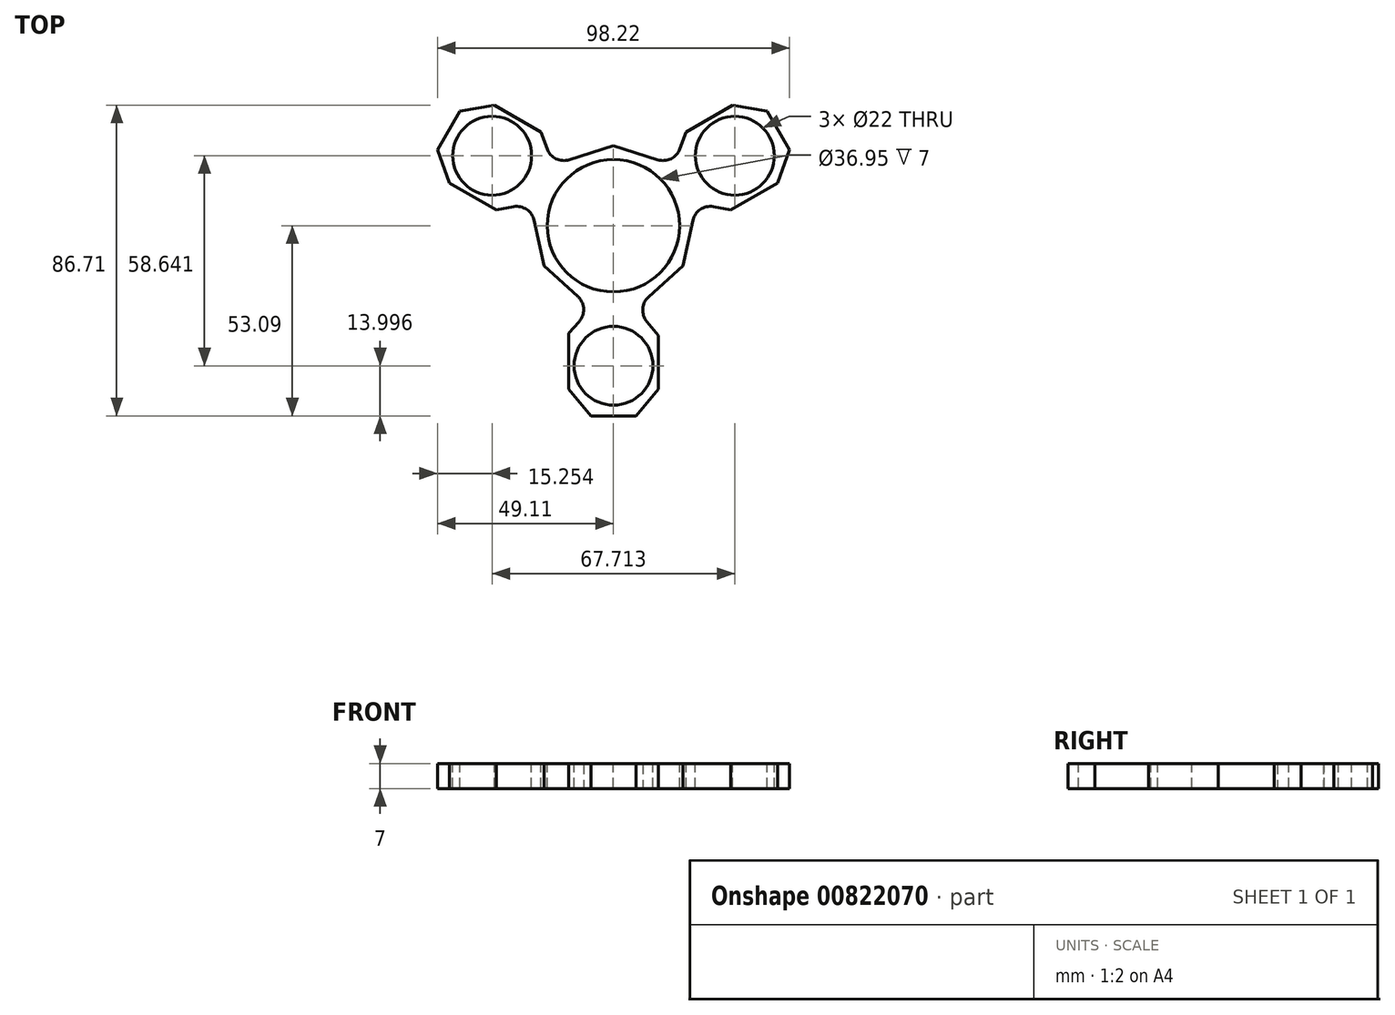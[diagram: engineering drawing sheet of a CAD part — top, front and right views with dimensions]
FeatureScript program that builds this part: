
annotation { "Feature Type Name" : "Feature", "Feature Type Description" : "" }
export const myFeature = defineFeature(function(context is Context, id is Id, definition is map)
    precondition{}
    {
        {
            var Q0;
            Q0=qCreatedBy(makeId("Top.planeOp"),FACE);
            var sketch = newSketch(context, id + "F0", { "sketchPlane" : qUnion([Q0])});
            skLineSegment(sketch, "E0", {"start": v(40, 0) * mm, "end": v(0, 69.28) * mm});
            skLineSegment(sketch, "E1", {"start": v(0, 69.28) * mm, "end": v(-40, 0) * mm});
            skLineSegment(sketch, "E2", {"start": v(40, 0) * mm, "end": v(-40, 0) * mm});
            skLineSegment(sketch, "E3", {"start": v(0, 69.28) * mm, "end": v(0, 0) * mm});
            skLineSegment(sketch, "E4", {"start": v(-40, 0) * mm, "end": v(20, 34.64) * mm});
            skLineSegment(sketch, "E5", {"start": v(40, 0) * mm, "end": v(-20, 34.64) * mm});
            skLineSegment(sketch, "E6", {"start": v(-20, 34.64) * mm, "end": v(0, 23.1) * mm});
            skSolve(sketch);
        }
        {
            var Q0;
            {var subQ3=sQuery(id+"F0.wireOp",EDGE,"E6");Q0=makeQuery(id+"F0.imprint","IMPRINT",FACE,{"disambiguationData":[TD([[makeQuery(id+"F0.imprint","IMPRINT",EDGE,{"derivedFrom":subQ3}),1.0]])]});}
            var Q1;
            {var subQ1=sQuery(id+"F0.wireOp",EDGE,"E0");var subQ3=sQuery(id+"F0.wireOp",EDGE,"E4");var subQ4=makeQuery(id+"F0.imprint","INTERSECT",VERTEX,{"derivedFrom":[subQ1,subQ3]});Q1=makeQuery(id+"F0.imprint","IMPRINT",FACE,{"disambiguationData":[TD([[makeQuery(id+"F0.imprint","IMPRINT",EDGE,{"disambiguationData":[TD([[subQ4,-1.0]])],"derivedFrom":subQ1}),1.0]])]});}
            var Q2;
            {var subQ0=sQuery(id+"F0.wireOp",EDGE,"E5");Q2=makeQuery(id+"F0.imprint","IMPRINT",FACE,{"disambiguationData":[TD([[makeQuery(id+"F0.imprint","IMPRINT",EDGE,{"derivedFrom":subQ0}),-1.0]])]});}
            var Q3;
            {var subQ0=sQuery(id+"F0.wireOp",EDGE,"E5");Q3=makeQuery(id+"F0.imprint","IMPRINT",FACE,{"disambiguationData":[TD([[makeQuery(id+"F0.imprint","IMPRINT",EDGE,{"derivedFrom":subQ0}),1.0]])]});}
            var Q4;
            {var subQ1=sQuery(id+"F0.wireOp",EDGE,"E2");var subQ3=sQuery(id+"F0.wireOp",EDGE,"E3");var subQ4=makeQuery(id+"F0.imprint","INTERSECT",VERTEX,{"derivedFrom":[subQ1,subQ3]});Q4=makeQuery(id+"F0.imprint","IMPRINT",FACE,{"disambiguationData":[TD([[makeQuery(id+"F0.imprint","IMPRINT",EDGE,{"disambiguationData":[TD([[subQ4,-1.0]])],"derivedFrom":subQ1}),-1.0]])]});}
            var Q5;
            {var subQ3=sQuery(id+"F0.wireOp",EDGE,"E6");Q5=makeQuery(id+"F0.imprint","IMPRINT",FACE,{"disambiguationData":[TD([[makeQuery(id+"F0.imprint","IMPRINT",EDGE,{"derivedFrom":subQ3}),-1.0]])]});}
            extrude(context, id + "F1", {"entities" : qUnion([Q0, Q1, Q2, Q3, Q4, Q5]), "depth" : 7 * mm, "offsetDistance" : 25 * mm});
        }
        {
            var Q0;
            Q0=makeQuery(id+"F1.opExtrude","SWEPT_BODY",BODY,{"disambiguationData":[OSD([sQuery(id+"F0.wireOp",EDGE,"E0"),sQuery(id+"F0.wireOp",EDGE,"E1"),sQuery(id+"F0.wireOp",EDGE,"E2")])]});
            var Q1;
            Q1=makeQuery(id+"F1.opExtrude","SWEPT_FACE",FACE,{"disambiguationData":[OSD([sQuery(id+"F0.wireOp",EDGE,"E2")])]});
            transform(context, id + "F2", {"entities" : qUnion([Q0]), "transformType" : TransformType.TRANSLATION_DISTANCE, "transformDirection" : qUnion([Q1]), "distance" : 23.1 * mm, "makeCopy" : false});
        }
        {
            var Q0;
            Q0=makeQuery(id+"F1.opExtrude","CAP_FACE",FACE,{"disambiguationData":[OSD([sQuery(id+"F0.wireOp",EDGE,"E0"),sQuery(id+"F0.wireOp",EDGE,"E1"),sQuery(id+"F0.wireOp",EDGE,"E2")])],"isStart":false});
            var sketch = newSketch(context, id + "F3", { "sketchPlane" : qUnion([Q0])});
            skCircle(sketch, "E7", {"center": v(0, 0) * mm, "radius": 18.48 * mm});
            skSolve(sketch);
        }
        {
            var Q0;
            Q0=makeQuery(id+"F3.imprint","IMPRINT",FACE,{"disambiguationData":[TD([[makeQuery(id+"F3.imprint","IMPRINT",EDGE,{"derivedFrom":sQuery(id+"F3.wireOp",EDGE,"E7")}),1.0]])]});
            extrude(context, id + "F4", {"entities" : qUnion([Q0]), "operationType" : NewBodyOperationType.REMOVE, "oppositeDirection" : true, "depth" : 25 * mm, "offsetDistance" : 25 * mm});
        }
        {
            var Q0;
            Q0=makeQuery(id+"F1.opExtrude","SWEPT_FACE",FACE,{"disambiguationData":[OSD([sQuery(id+"F0.wireOp",EDGE,"E2")])]});
            var sketch = newSketch(context, id + "F5", { "sketchPlane" : qUnion([Q0])});
            skPoint(sketch, "E8.middle", {"position": v(0, 0) * mm});
            skLineSegment(sketch, "E9", {"start": v(-12.5, 7) * mm, "end": v(12.5, 7) * mm});
            skPoint(sketch, "E9.endSnap0", {"position": v(12.5, 0) * mm});
            skLineSegment(sketch, "E10", {"start": v(12.5, 0) * mm, "end": v(-12.5, 0) * mm});
            skLineSegment(sketch, "E11", {"start": v(-12.5, 7) * mm, "end": v(-12.5, 0) * mm});
            skLineSegment(sketch, "E12", {"start": v(12.5, 0) * mm, "end": v(12.5, 7) * mm});
            skSolve(sketch);
        }
        {
            var Q0;
            Q0=makeQuery(id+"F5.imprint","IMPRINT",FACE,{"disambiguationData":[TD([[makeQuery(id+"F5.imprint","IMPRINT",EDGE,{"derivedFrom":sQuery(id+"F5.wireOp",EDGE,"E9")}),1.0]])]});
            extrude(context, id + "F6", {"entities" : qUnion([Q0]), "operationType" : NewBodyOperationType.ADD, "depth" : 30 * mm, "offsetDistance" : 25 * mm});
        }
        {
            var Q0;
            Q0=makeQuery(id+"F1.opExtrude","SWEPT_FACE",FACE,{"disambiguationData":[OSD([sQuery(id+"F0.wireOp",EDGE,"E0")])]});
            var sketch = newSketch(context, id + "F7", { "sketchPlane" : qUnion([Q0])});
            skLineSegment(sketch, "E13.bottom", {"start": v(12.5, 7) * mm, "end": v(-12.5, 7) * mm});
            skPoint(sketch, "E13.middle", {"position": v(0, 0) * mm});
            skLineSegment(sketch, "E14", {"start": v(-12.5, 0) * mm, "end": v(12.5, 0) * mm});
            skLineSegment(sketch, "E15", {"start": v(-12.5, 7) * mm, "end": v(-12.5, 0) * mm});
            skLineSegment(sketch, "E16", {"start": v(12.5, 7) * mm, "end": v(12.5, 0) * mm});
            skSolve(sketch);
        }
        {
            var Q0;
            Q0 = qSketchRegion(id + "F7", true);
            extrude(context, id + "F8", {"entities" : qUnion([Q0]), "operationType" : NewBodyOperationType.ADD, "depth" : 30 * mm, "offsetDistance" : 25 * mm});
        }
        {
            var Q0;
            Q0=makeQuery(id+"F1.opExtrude","SWEPT_FACE",FACE,{"disambiguationData":[OSD([sQuery(id+"F0.wireOp",EDGE,"E1")])]});
            var sketch = newSketch(context, id + "F9", { "sketchPlane" : qUnion([Q0])});
            skLineSegment(sketch, "E17.bottom", {"start": v(12.5, 0) * mm, "end": v(-12.5, 0) * mm});
            skPoint(sketch, "E17.middle", {"position": v(0, 1.96) * mm});
            skLineSegment(sketch, "E18", {"start": v(-12.5, 0) * mm, "end": v(-12.5, 7) * mm});
            skLineSegment(sketch, "E19", {"start": v(12.5, 0) * mm, "end": v(12.5, 7) * mm});
            skLineSegment(sketch, "E20", {"start": v(12.5, 7) * mm, "end": v(-12.5, 7) * mm});
            skLineSegment(sketch, "E21", {"start": v(-12.5, 7) * mm, "end": v(12.5, 7) * mm});
            skSolve(sketch);
        }
        {
            var Q0;
            Q0=makeQuery(id+"F9.imprint","IMPRINT",FACE,{"disambiguationData":[TD([[makeQuery(id+"F9.imprint","IMPRINT",EDGE,{"derivedFrom":sQuery(id+"F9.wireOp",EDGE,"E17.bottom")}),1.0]])]});
            extrude(context, id + "F10", {"entities" : qUnion([Q0]), "operationType" : NewBodyOperationType.ADD, "depth" : 30 * mm, "offsetDistance" : 25 * mm});
        }
        {
            var Q0;
            Q0=makeQuery(id+"F10.boolean.opBoolean","MERGE",FACE,{"derivedFrom":[makeQuery(id+"F8.boolean.opBoolean","MERGE",FACE,{"derivedFrom":[makeQuery(id+"F6.boolean.opBoolean","MERGE",FACE,{"derivedFrom":[makeQuery(id+"F1.opExtrude","CAP_FACE",FACE,{"disambiguationData":[OSD([sQuery(id+"F0.wireOp",EDGE,"E0"),sQuery(id+"F0.wireOp",EDGE,"E1"),sQuery(id+"F0.wireOp",EDGE,"E2")])],"isStart":false}),makeQuery(id+"F6.opExtrude","SWEPT_FACE",FACE,{"disambiguationData":[OSD([sQuery(id+"F5.wireOp",EDGE,"E9")])]})]}),makeQuery(id+"F8.opExtrude","SWEPT_FACE",FACE,{"disambiguationData":[OSD([sQuery(id+"F7.wireOp",EDGE,"E13.bottom")])]})]}),makeQuery(id+"F10.opExtrude","SWEPT_FACE",FACE,{"disambiguationData":[OSD([sQuery(id+"F9.wireOp",EDGE,"E21")])]})]});
            var sketch = newSketch(context, id + "F11", { "sketchPlane" : qUnion([Q0])});
            skLineSegment(sketch, "E22", {"start": v(-26.25, 0.72) * mm, "end": v(-12.5, -23.1) * mm});
            skLineSegment(sketch, "E23", {"start": v(-13.75, 22.37) * mm, "end": v(13.75, 22.37) * mm});
            skLineSegment(sketch, "E24", {"start": v(26.25, 0.72) * mm, "end": v(12.5, -23.1) * mm});
            skSolve(sketch);
        }
        {
            var Q0;
            Q0 = qSketchRegion(id + "F11", true);
            var Q1;
            Q1=makeQuery(id+"F11.imprint","IMPRINT",FACE,{"disambiguationData":[TD([[makeQuery(id+"F11.imprint","IMPRINT",EDGE,{"derivedFrom":sQuery(id+"F11.wireOp",EDGE,"E23")}),1.0]])]});
            var Q2;
            Q2=makeQuery(id+"F11.imprint","IMPRINT",FACE,{"disambiguationData":[TD([[makeQuery(id+"F11.imprint","IMPRINT",EDGE,{"derivedFrom":sQuery(id+"F11.wireOp",EDGE,"E24")}),1.0]])]});
            var Q3;
            Q3=makeQuery(id+"F11.imprint","IMPRINT",FACE,{"disambiguationData":[TD([[makeQuery(id+"F11.imprint","IMPRINT",EDGE,{"derivedFrom":sQuery(id+"F11.wireOp",EDGE,"E22")}),-1.0]])]});
            extrude(context, id + "F12", {"entities" : qUnion([Q0, Q1, Q2, Q3]), "operationType" : NewBodyOperationType.REMOVE, "oppositeDirection" : true, "depth" : 25 * mm, "offsetDistance" : 25 * mm});
        }
        {
            var Q0;
            Q0=makeQuery(id+"F10.boolean.opBoolean","MERGE",FACE,{"derivedFrom":[makeQuery(id+"F8.boolean.opBoolean","MERGE",FACE,{"derivedFrom":[makeQuery(id+"F6.boolean.opBoolean","MERGE",FACE,{"derivedFrom":[makeQuery(id+"F1.opExtrude","CAP_FACE",FACE,{"disambiguationData":[OSD([sQuery(id+"F0.wireOp",EDGE,"E0"),sQuery(id+"F0.wireOp",EDGE,"E1"),sQuery(id+"F0.wireOp",EDGE,"E2")])],"isStart":false}),makeQuery(id+"F6.opExtrude","SWEPT_FACE",FACE,{"disambiguationData":[OSD([sQuery(id+"F5.wireOp",EDGE,"E9")])]})]}),makeQuery(id+"F8.opExtrude","SWEPT_FACE",FACE,{"disambiguationData":[OSD([sQuery(id+"F7.wireOp",EDGE,"E13.bottom")])]})]}),makeQuery(id+"F10.opExtrude","SWEPT_FACE",FACE,{"disambiguationData":[OSD([sQuery(id+"F9.wireOp",EDGE,"E21")])]})]});
            var sketch = newSketch(context, id + "F13", { "sketchPlane" : qUnion([Q0])});
            skLineSegment(sketch, "E25", {"start": v(0, -53.1) * mm, "end": v(0, -50.1) * mm});
            skLineSegment(sketch, "E26", {"start": v(0, -53.1) * mm, "end": v(0, -39.1) * mm});
            skCircle(sketch, "E27", {"center": v(0, -39.1) * mm, "radius": 11 * mm});
            skLineSegment(sketch, "E28", {"start": v(-45.98, 26.55) * mm, "end": v(-33.86, 19.55) * mm});
            skLineSegment(sketch, "E29", {"start": v(45.98, 26.55) * mm, "end": v(33.86, 19.55) * mm});
            skCircle(sketch, "E30", {"center": v(-33.86, 19.55) * mm, "radius": 11 * mm});
            skCircle(sketch, "E31", {"center": v(33.86, 19.55) * mm, "radius": 11 * mm});
            skSolve(sketch);
        }
        {
            var Q0;
            Q0=makeQuery(id+"F13.imprint","IMPRINT",FACE,{"disambiguationData":[TD([[makeQuery(id+"F13.imprint","IMPRINT",EDGE,{"derivedFrom":sQuery(id+"F13.wireOp",EDGE,"E30")}),1.0]])]});
            var Q1;
            Q1=makeQuery(id+"F13.imprint","IMPRINT",FACE,{"disambiguationData":[TD([[makeQuery(id+"F13.imprint","IMPRINT",EDGE,{"derivedFrom":sQuery(id+"F13.wireOp",EDGE,"E31")}),1.0]])]});
            var Q2;
            Q2=makeQuery(id+"F13.imprint","IMPRINT",FACE,{"disambiguationData":[TD([[makeQuery(id+"F13.imprint","IMPRINT",EDGE,{"derivedFrom":sQuery(id+"F13.wireOp",EDGE,"E27")}),1.0]])]});
            extrude(context, id + "F14", {"entities" : qUnion([Q0, Q1, Q2]), "operationType" : NewBodyOperationType.REMOVE, "oppositeDirection" : true, "depth" : 25 * mm, "offsetDistance" : 25 * mm});
        }
        {
            var Q0;
            Q0=makeQuery(id+"F10.boolean.opBoolean","MERGE",FACE,{"derivedFrom":[makeQuery(id+"F8.boolean.opBoolean","MERGE",FACE,{"derivedFrom":[makeQuery(id+"F6.boolean.opBoolean","MERGE",FACE,{"derivedFrom":[makeQuery(id+"F1.opExtrude","CAP_FACE",FACE,{"disambiguationData":[OSD([sQuery(id+"F0.wireOp",EDGE,"E0"),sQuery(id+"F0.wireOp",EDGE,"E1"),sQuery(id+"F0.wireOp",EDGE,"E2")])],"isStart":false}),makeQuery(id+"F6.opExtrude","SWEPT_FACE",FACE,{"disambiguationData":[OSD([sQuery(id+"F5.wireOp",EDGE,"E9")])]})]}),makeQuery(id+"F8.opExtrude","SWEPT_FACE",FACE,{"disambiguationData":[OSD([sQuery(id+"F7.wireOp",EDGE,"E13.bottom")])]})]}),makeQuery(id+"F10.opExtrude","SWEPT_FACE",FACE,{"disambiguationData":[OSD([sQuery(id+"F9.wireOp",EDGE,"E21")])]})]});
            var sketch = newSketch(context, id + "F15", { "sketchPlane" : qUnion([Q0])});
            skLineSegment(sketch, "E32", {"start": v(-26.25, 0.72) * mm, "end": v(-13.75, 22.37) * mm});
            skLineSegment(sketch, "E33", {"start": v(13.75, 22.37) * mm, "end": v(26.25, 0.72) * mm});
            skLineSegment(sketch, "E34", {"start": v(12.5, -23.1) * mm, "end": v(-12.5, -23.1) * mm});
            skLineSegment(sketch, "E35", {"start": v(-26.25, 0.72) * mm, "end": v(-20, 11.55) * mm});
            skLineSegment(sketch, "E36", {"start": v(-20, 11.55) * mm, "end": v(-13.75, 22.37) * mm});
            skLineSegment(sketch, "E37", {"start": v(13.75, 22.37) * mm, "end": v(20, 11.55) * mm});
            skLineSegment(sketch, "E38", {"start": v(20, 11.55) * mm, "end": v(26.25, 0.72) * mm});
            skLineSegment(sketch, "E39", {"start": v(12.5, -23.1) * mm, "end": v(0, -23.1) * mm});
            skLineSegment(sketch, "E40", {"start": v(0, -23.1) * mm, "end": v(-12.5, -23.1) * mm});
            skLineSegment(sketch, "E41", {"start": v(-26.74, 29.87) * mm, "end": v(-13.75, 22.37) * mm});
            skLineSegment(sketch, "E42", {"start": v(-39.24, 8.22) * mm, "end": v(-26.25, 0.72) * mm});
            skLineSegment(sketch, "E43", {"start": v(-12.5, -38.1) * mm, "end": v(-12.5, -23.1) * mm});
            skLineSegment(sketch, "E44", {"start": v(12.5, -38.1) * mm, "end": v(12.5, -23.1) * mm});
            skLineSegment(sketch, "E45", {"start": v(39.24, 8.22) * mm, "end": v(26.25, 0.72) * mm});
            skLineSegment(sketch, "E46", {"start": v(13.75, 22.37) * mm, "end": v(26.74, 29.87) * mm});
            skLineSegment(sketch, "E47", {"start": v(-20.25, 26.12) * mm, "end": v(-16.88, 16.96) * mm});
            skLineSegment(sketch, "E48", {"start": v(-16.88, 16.96) * mm, "end": v(0, 22.37) * mm});
            skLineSegment(sketch, "E49", {"start": v(0, 22.37) * mm, "end": v(16.87, 16.96) * mm});
            skLineSegment(sketch, "E50", {"start": v(16.87, 16.96) * mm, "end": v(20.25, 26.12) * mm});
            skLineSegment(sketch, "E51", {"start": v(-32.75, 4.47) * mm, "end": v(-23.13, 6.13) * mm});
            skLineSegment(sketch, "E52", {"start": v(-23.13, 6.13) * mm, "end": v(-19.38, -11.19) * mm});
            skLineSegment(sketch, "E53", {"start": v(-19.38, -11.19) * mm, "end": v(-6.25, -23.1) * mm});
            skLineSegment(sketch, "E54", {"start": v(-6.25, -23.1) * mm, "end": v(-12.5, -29.98) * mm});
            skLineSegment(sketch, "E55", {"start": v(12.5, -30.6) * mm, "end": v(6.25, -23.1) * mm});
            skLineSegment(sketch, "E56", {"start": v(6.25, -23.1) * mm, "end": v(19.38, -11.19) * mm});
            skLineSegment(sketch, "E57", {"start": v(19.38, -11.19) * mm, "end": v(23.12, 6.13) * mm});
            skLineSegment(sketch, "E58", {"start": v(23.12, 6.13) * mm, "end": v(32.75, 4.47) * mm});
            skLineSegment(sketch, "E59", {"start": v(-52.23, 15.72) * mm, "end": v(-39.24, 8.22) * mm});
            skLineSegment(sketch, "E60", {"start": v(-39.73, 37.37) * mm, "end": v(-26.74, 29.87) * mm});
            skLineSegment(sketch, "E61", {"start": v(39.73, 37.37) * mm, "end": v(26.74, 29.87) * mm});
            skLineSegment(sketch, "E62", {"start": v(52.23, 15.72) * mm, "end": v(39.24, 8.22) * mm});
            skLineSegment(sketch, "E63", {"start": v(12.5, -53.1) * mm, "end": v(12.5, -38.1) * mm});
            skLineSegment(sketch, "E64", {"start": v(-12.5, -53.1) * mm, "end": v(-12.5, -38.1) * mm});
            skLineSegment(sketch, "E65", {"start": v(-12.5, -53.1) * mm, "end": v(0, -53.1) * mm});
            skLineSegment(sketch, "E66", {"start": v(0, -53.1) * mm, "end": v(12.5, -53.1) * mm});
            skLineSegment(sketch, "E67", {"start": v(-39.73, 37.37) * mm, "end": v(-45.98, 26.55) * mm});
            skLineSegment(sketch, "E68", {"start": v(-45.98, 26.55) * mm, "end": v(-52.23, 15.72) * mm});
            skLineSegment(sketch, "E69", {"start": v(39.73, 37.37) * mm, "end": v(45.98, 26.55) * mm});
            skLineSegment(sketch, "E70", {"start": v(45.98, 26.55) * mm, "end": v(52.23, 15.72) * mm});
            skLineSegment(sketch, "E71", {"start": v(33.24, 33.62) * mm, "end": v(42.86, 31.96) * mm});
            skLineSegment(sketch, "E72", {"start": v(42.86, 31.96) * mm, "end": v(49.1, 21.13) * mm});
            skLineSegment(sketch, "E73", {"start": v(49.1, 21.13) * mm, "end": v(45.74, 11.97) * mm});
            skLineSegment(sketch, "E74", {"start": v(-42.86, 31.96) * mm, "end": v(-33.24, 33.62) * mm});
            skLineSegment(sketch, "E75", {"start": v(-49.1, 21.13) * mm, "end": v(-45.74, 11.97) * mm});
            skLineSegment(sketch, "E76", {"start": v(-12.5, -45.6) * mm, "end": v(-6.25, -53.1) * mm});
            skLineSegment(sketch, "E77", {"start": v(-6.25, -53.1) * mm, "end": v(6.25, -53.1) * mm});
            skLineSegment(sketch, "E78", {"start": v(6.25, -53.1) * mm, "end": v(12.5, -45.6) * mm});
            skSolve(sketch);
        }
        {
            var Q0;
            {var subQ3=sQuery(id+"F15.wireOp",EDGE,"E47");Q0=makeQuery(id+"F15.imprint","IMPRINT",FACE,{"disambiguationData":[TD([[makeQuery(id+"F15.imprint","IMPRINT",EDGE,{"derivedFrom":subQ3}),1.0]])]});}
            var Q1;
            {var subQ3=sQuery(id+"F15.wireOp",EDGE,"E48");Q1=makeQuery(id+"F15.imprint","IMPRINT",FACE,{"disambiguationData":[TD([[makeQuery(id+"F15.imprint","IMPRINT",EDGE,{"derivedFrom":subQ3}),1.0]])]});}
            var Q2;
            {var subQ3=sQuery(id+"F15.wireOp",EDGE,"E49");Q2=makeQuery(id+"F15.imprint","IMPRINT",FACE,{"disambiguationData":[TD([[makeQuery(id+"F15.imprint","IMPRINT",EDGE,{"derivedFrom":subQ3}),1.0]])]});}
            var Q3;
            {var subQ3=sQuery(id+"F15.wireOp",EDGE,"E50");Q3=makeQuery(id+"F15.imprint","IMPRINT",FACE,{"disambiguationData":[TD([[makeQuery(id+"F15.imprint","IMPRINT",EDGE,{"derivedFrom":subQ3}),1.0]])]});}
            var Q4;
            {var subQ3=sQuery(id+"F15.wireOp",EDGE,"E58");Q4=makeQuery(id+"F15.imprint","IMPRINT",FACE,{"disambiguationData":[TD([[makeQuery(id+"F15.imprint","IMPRINT",EDGE,{"derivedFrom":subQ3}),-1.0]])]});}
            var Q5;
            {var subQ3=sQuery(id+"F15.wireOp",EDGE,"E57");Q5=makeQuery(id+"F15.imprint","IMPRINT",FACE,{"disambiguationData":[TD([[makeQuery(id+"F15.imprint","IMPRINT",EDGE,{"derivedFrom":subQ3}),-1.0]])]});}
            var Q6;
            {var subQ3=sQuery(id+"F15.wireOp",EDGE,"E56");Q6=makeQuery(id+"F15.imprint","IMPRINT",FACE,{"disambiguationData":[TD([[makeQuery(id+"F15.imprint","IMPRINT",EDGE,{"derivedFrom":subQ3}),-1.0]])]});}
            var Q7;
            {var subQ3=sQuery(id+"F15.wireOp",EDGE,"E55");Q7=makeQuery(id+"F15.imprint","IMPRINT",FACE,{"disambiguationData":[TD([[makeQuery(id+"F15.imprint","IMPRINT",EDGE,{"derivedFrom":subQ3}),-1.0]])]});}
            var Q8;
            {var subQ3=sQuery(id+"F15.wireOp",EDGE,"E54");Q8=makeQuery(id+"F15.imprint","IMPRINT",FACE,{"disambiguationData":[TD([[makeQuery(id+"F15.imprint","IMPRINT",EDGE,{"derivedFrom":subQ3}),-1.0]])]});}
            var Q9;
            {var subQ3=sQuery(id+"F15.wireOp",EDGE,"E53");Q9=makeQuery(id+"F15.imprint","IMPRINT",FACE,{"disambiguationData":[TD([[makeQuery(id+"F15.imprint","IMPRINT",EDGE,{"derivedFrom":subQ3}),-1.0]])]});}
            var Q10;
            {var subQ3=sQuery(id+"F15.wireOp",EDGE,"E52");Q10=makeQuery(id+"F15.imprint","IMPRINT",FACE,{"disambiguationData":[TD([[makeQuery(id+"F15.imprint","IMPRINT",EDGE,{"derivedFrom":subQ3}),-1.0]])]});}
            var Q11;
            {var subQ3=sQuery(id+"F15.wireOp",EDGE,"E51");Q11=makeQuery(id+"F15.imprint","IMPRINT",FACE,{"disambiguationData":[TD([[makeQuery(id+"F15.imprint","IMPRINT",EDGE,{"derivedFrom":subQ3}),-1.0]])]});}
            var Q12;
            {var subQ3=sQuery(id+"F15.wireOp",EDGE,"E75");Q12=makeQuery(id+"F15.imprint","IMPRINT",FACE,{"disambiguationData":[TD([[makeQuery(id+"F15.imprint","IMPRINT",EDGE,{"derivedFrom":subQ3}),-1.0]])]});}
            var Q13;
            {var subQ3=sQuery(id+"F15.wireOp",EDGE,"E74");Q13=makeQuery(id+"F15.imprint","IMPRINT",FACE,{"disambiguationData":[TD([[makeQuery(id+"F15.imprint","IMPRINT",EDGE,{"derivedFrom":subQ3}),1.0]])]});}
            var Q14;
            {var subQ0=sQuery(id+"F15.wireOp",EDGE,"E69");Q14=makeQuery(id+"F15.imprint","IMPRINT",FACE,{"disambiguationData":[TD([[makeQuery(id+"F15.imprint","IMPRINT",EDGE,{"derivedFrom":subQ0}),1.0]])]});}
            var Q15;
            {var subQ0=sQuery(id+"F15.wireOp",EDGE,"E70");Q15=makeQuery(id+"F15.imprint","IMPRINT",FACE,{"disambiguationData":[TD([[makeQuery(id+"F15.imprint","IMPRINT",EDGE,{"derivedFrom":subQ0}),1.0]])]});}
            var Q16;
            {var subQ0=sQuery(id+"F15.wireOp",EDGE,"E66");Q16=makeQuery(id+"F15.imprint","IMPRINT",FACE,{"disambiguationData":[TD([[makeQuery(id+"F15.imprint","IMPRINT",EDGE,{"derivedFrom":subQ0}),-1.0]])]});}
            var Q17;
            {var subQ0=sQuery(id+"F15.wireOp",EDGE,"E65");Q17=makeQuery(id+"F15.imprint","IMPRINT",FACE,{"disambiguationData":[TD([[makeQuery(id+"F15.imprint","IMPRINT",EDGE,{"derivedFrom":subQ0}),-1.0]])]});}
            extrude(context, id + "F16", {"entities" : qUnion([Q0, Q1, Q2, Q3, Q4, Q5, Q6, Q7, Q8, Q9, Q10, Q11, Q12, Q13, Q14, Q15, Q16, Q17]), "operationType" : NewBodyOperationType.REMOVE, "oppositeDirection" : true, "depth" : 25 * mm, "offsetDistance" : 25 * mm});
        }
        {
            var Q0;
            Q0=makeQuery(id+"F16.boolean.opBoolean","COPY",EDGE,{"derivedFrom":makeQuery(id+"F16.opExtrude","SWEPT_EDGE",EDGE,{"disambiguationData":[OSD([sQuery(id+"F15.wireOp",EDGE,"E66"),sQuery(id+"F15.wireOp",EDGE,"E77"),sQuery(id+"F15.wireOp",EDGE,"E78")])]})});
            var Q1;
            Q1=makeQuery(id+"F16.boolean.opBoolean","COPY",EDGE,{"derivedFrom":makeQuery(id+"F16.opExtrude","SWEPT_EDGE",EDGE,{"disambiguationData":[OSD([sQuery(id+"F15.wireOp",EDGE,"E63"),sQuery(id+"F15.wireOp",EDGE,"E78")])]})});
            var Q2;
            Q2=makeQuery(id+"F16.boolean.opBoolean","COPY",EDGE,{"derivedFrom":makeQuery(id+"F16.opExtrude","SWEPT_EDGE",EDGE,{"disambiguationData":[OSD([sQuery(id+"F15.wireOp",EDGE,"E44"),sQuery(id+"F15.wireOp",EDGE,"E55")])]})});
            var Q3;
            Q3=makeQuery(id+"F16.boolean.opBoolean","COPY",EDGE,{"derivedFrom":makeQuery(id+"F16.opExtrude","SWEPT_EDGE",EDGE,{"disambiguationData":[OSD([sQuery(id+"F15.wireOp",EDGE,"E65"),sQuery(id+"F15.wireOp",EDGE,"E76"),sQuery(id+"F15.wireOp",EDGE,"E77")])]})});
            var Q4;
            {var subQ0=sQuery(id+"F15.wireOp",EDGE,"E57");var subQ1=sQuery(id+"F15.wireOp",EDGE,"E56");var subQ2=sQuery(id+"F11.wireOp",EDGE,"E24");Q4=makeQuery(id+"F16.boolean.opBoolean","TWEAK_EDGE",EDGE,{"derivedFrom":[makeQuery(id+"F16.opExtrude","SWEPT_EDGE",EDGE,{"disambiguationData":[OSD([subQ2,subQ1,subQ0]),OD(0.0)]}),makeQuery(id+"F16.opExtrude","SWEPT_EDGE",EDGE,{"disambiguationData":[OSD([subQ2,subQ1,subQ0]),OD(1.0)]})]});}
            var Q5;
            Q5=makeQuery(id+"F16.boolean.opBoolean","COPY",EDGE,{"derivedFrom":makeQuery(id+"F16.opExtrude","SWEPT_EDGE",EDGE,{"disambiguationData":[OSD([sQuery(id+"F15.wireOp",EDGE,"E38"),sQuery(id+"F15.wireOp",EDGE,"E57"),sQuery(id+"F15.wireOp",EDGE,"E58")])]})});
            var Q6;
            Q6=makeQuery(id+"F16.boolean.opBoolean","COPY",EDGE,{"derivedFrom":makeQuery(id+"F16.opExtrude","SWEPT_EDGE",EDGE,{"disambiguationData":[OSD([sQuery(id+"F15.wireOp",EDGE,"E45"),sQuery(id+"F15.wireOp",EDGE,"E58")])]})});
            var Q7;
            Q7=makeQuery(id+"F16.boolean.opBoolean","COPY",EDGE,{"derivedFrom":makeQuery(id+"F16.opExtrude","SWEPT_EDGE",EDGE,{"disambiguationData":[OSD([sQuery(id+"F15.wireOp",EDGE,"E62"),sQuery(id+"F15.wireOp",EDGE,"E73")])]})});
            var Q8;
            Q8=makeQuery(id+"F16.boolean.opBoolean","COPY",EDGE,{"derivedFrom":makeQuery(id+"F16.opExtrude","SWEPT_EDGE",EDGE,{"disambiguationData":[OSD([sQuery(id+"F15.wireOp",EDGE,"E39"),sQuery(id+"F15.wireOp",EDGE,"E55"),sQuery(id+"F15.wireOp",EDGE,"E56")])]})});
            var Q9;
            Q9=makeQuery(id+"F16.boolean.opBoolean","COPY",EDGE,{"derivedFrom":makeQuery(id+"F16.opExtrude","SWEPT_EDGE",EDGE,{"disambiguationData":[OSD([sQuery(id+"F15.wireOp",EDGE,"E70"),sQuery(id+"F15.wireOp",EDGE,"E72"),sQuery(id+"F15.wireOp",EDGE,"E73")])]})});
            var Q10;
            Q10=makeQuery(id+"F16.boolean.opBoolean","COPY",EDGE,{"derivedFrom":makeQuery(id+"F16.opExtrude","SWEPT_EDGE",EDGE,{"disambiguationData":[OSD([sQuery(id+"F15.wireOp",EDGE,"E69"),sQuery(id+"F15.wireOp",EDGE,"E71"),sQuery(id+"F15.wireOp",EDGE,"E72")])]})});
            var Q11;
            Q11=makeQuery(id+"F16.boolean.opBoolean","COPY",EDGE,{"derivedFrom":makeQuery(id+"F16.opExtrude","SWEPT_EDGE",EDGE,{"disambiguationData":[OSD([sQuery(id+"F15.wireOp",EDGE,"E61"),sQuery(id+"F15.wireOp",EDGE,"E71")])]})});
            var Q12;
            Q12=makeQuery(id+"F16.boolean.opBoolean","COPY",EDGE,{"derivedFrom":makeQuery(id+"F16.opExtrude","SWEPT_EDGE",EDGE,{"disambiguationData":[OSD([sQuery(id+"F15.wireOp",EDGE,"E46"),sQuery(id+"F15.wireOp",EDGE,"E50")])]})});
            var Q13;
            Q13=makeQuery(id+"F16.boolean.opBoolean","COPY",EDGE,{"derivedFrom":makeQuery(id+"F16.opExtrude","SWEPT_EDGE",EDGE,{"disambiguationData":[OSD([sQuery(id+"F15.wireOp",EDGE,"E37"),sQuery(id+"F15.wireOp",EDGE,"E49"),sQuery(id+"F15.wireOp",EDGE,"E50")])]})});
            var Q14;
            {var subQ0=sQuery(id+"F15.wireOp",EDGE,"E49");var subQ1=sQuery(id+"F15.wireOp",EDGE,"E48");var subQ2=sQuery(id+"F11.wireOp",EDGE,"E23");Q14=makeQuery(id+"F16.boolean.opBoolean","TWEAK_EDGE",EDGE,{"derivedFrom":[makeQuery(id+"F16.opExtrude","SWEPT_EDGE",EDGE,{"disambiguationData":[OSD([subQ2,subQ1,subQ0]),OD(0.0)]}),makeQuery(id+"F16.opExtrude","SWEPT_EDGE",EDGE,{"disambiguationData":[OSD([subQ2,subQ1,subQ0]),OD(1.0)]})]});}
            var Q15;
            Q15=makeQuery(id+"F16.boolean.opBoolean","COPY",EDGE,{"derivedFrom":makeQuery(id+"F16.opExtrude","SWEPT_EDGE",EDGE,{"disambiguationData":[OSD([sQuery(id+"F15.wireOp",EDGE,"E60"),sQuery(id+"F15.wireOp",EDGE,"E74")])]})});
            var Q16;
            Q16=makeQuery(id+"F16.boolean.opBoolean","COPY",EDGE,{"derivedFrom":makeQuery(id+"F16.opExtrude","SWEPT_EDGE",EDGE,{"disambiguationData":[OSD([sQuery(id+"F15.wireOp",EDGE,"E43"),sQuery(id+"F15.wireOp",EDGE,"E54")])]})});
            var Q17;
            Q17=makeQuery(id+"F16.boolean.opBoolean","COPY",EDGE,{"derivedFrom":makeQuery(id+"F16.opExtrude","SWEPT_EDGE",EDGE,{"disambiguationData":[OSD([sQuery(id+"F15.wireOp",EDGE,"E67"),sQuery(id+"F15.wireOp",EDGE,"E74")])]})});
            var Q18;
            Q18=makeQuery(id+"F16.boolean.opBoolean","COPY",EDGE,{"derivedFrom":makeQuery(id+"F16.opExtrude","SWEPT_EDGE",EDGE,{"disambiguationData":[OSD([sQuery(id+"F15.wireOp",EDGE,"E68"),sQuery(id+"F15.wireOp",EDGE,"E75")])]})});
            var Q19;
            Q19=makeQuery(id+"F16.boolean.opBoolean","COPY",EDGE,{"derivedFrom":makeQuery(id+"F16.opExtrude","SWEPT_EDGE",EDGE,{"disambiguationData":[OSD([sQuery(id+"F15.wireOp",EDGE,"E36"),sQuery(id+"F15.wireOp",EDGE,"E47"),sQuery(id+"F15.wireOp",EDGE,"E48")])]})});
            var Q20;
            {var subQ0=sQuery(id+"F15.wireOp",EDGE,"E53");var subQ1=sQuery(id+"F15.wireOp",EDGE,"E52");var subQ2=sQuery(id+"F11.wireOp",EDGE,"E22");Q20=makeQuery(id+"F16.boolean.opBoolean","TWEAK_EDGE",EDGE,{"derivedFrom":[makeQuery(id+"F16.opExtrude","SWEPT_EDGE",EDGE,{"disambiguationData":[OSD([subQ2,subQ1,subQ0]),OD(0.0)]}),makeQuery(id+"F16.opExtrude","SWEPT_EDGE",EDGE,{"disambiguationData":[OSD([subQ2,subQ1,subQ0]),OD(1.0)]})]});}
            var Q21;
            Q21=makeQuery(id+"F16.boolean.opBoolean","COPY",EDGE,{"derivedFrom":makeQuery(id+"F16.opExtrude","SWEPT_EDGE",EDGE,{"disambiguationData":[OSD([sQuery(id+"F15.wireOp",EDGE,"E35"),sQuery(id+"F15.wireOp",EDGE,"E51"),sQuery(id+"F15.wireOp",EDGE,"E52")])]})});
            var Q22;
            Q22=makeQuery(id+"F16.boolean.opBoolean","COPY",EDGE,{"derivedFrom":makeQuery(id+"F16.opExtrude","SWEPT_EDGE",EDGE,{"disambiguationData":[OSD([sQuery(id+"F15.wireOp",EDGE,"E42"),sQuery(id+"F15.wireOp",EDGE,"E51")])]})});
            var Q23;
            Q23=makeQuery(id+"F16.boolean.opBoolean","COPY",EDGE,{"derivedFrom":makeQuery(id+"F16.opExtrude","SWEPT_EDGE",EDGE,{"disambiguationData":[OSD([sQuery(id+"F15.wireOp",EDGE,"E59"),sQuery(id+"F15.wireOp",EDGE,"E75")])]})});
            var Q24;
            Q24=makeQuery(id+"F16.boolean.opBoolean","COPY",EDGE,{"derivedFrom":makeQuery(id+"F16.opExtrude","SWEPT_EDGE",EDGE,{"disambiguationData":[OSD([sQuery(id+"F15.wireOp",EDGE,"E40"),sQuery(id+"F15.wireOp",EDGE,"E53"),sQuery(id+"F15.wireOp",EDGE,"E54")])]})});
            fillet(context, id + "F17", {"entities" : qUnion([Q0, Q1, Q2, Q3, Q4, Q5, Q6, Q7, Q8, Q9, Q10, Q11, Q12, Q13, Q14, Q15, Q16, Q17, Q18, Q19, Q20, Q21, Q22, Q23, Q24]), "radius" : 5 * mm, "tangentPropagation" : true, "allowEdgeOverflow" : false});
        }
    });
